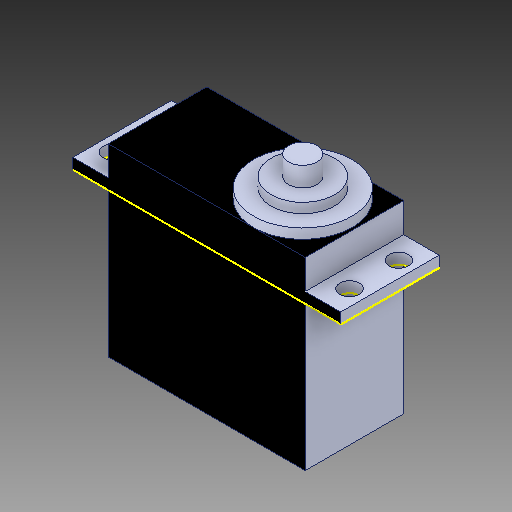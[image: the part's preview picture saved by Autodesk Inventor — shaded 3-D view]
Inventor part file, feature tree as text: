
AUTODESK INVENTOR PART (.ipt)
format: ipt  version: 2018 (Build 220112000, 112)  size: 164,864 bytes
history: native  units: mm
features: other x3, sketch x1
ambient origin geometry x8: Origin, YZ Plane, XZ Plane, XY Plane, X Axis, Y Axis, Z Axis, Center Point
bodies: Solid1 (feature_tree)
feature tree (4):
  other  "SERVOMG996R.ipt"
  other  "Solid1::SERVOMG996R.ipt"
  other  "TaggingFeature1"
  sketch  "Sketch7"  dims[d0=10.0mm]
